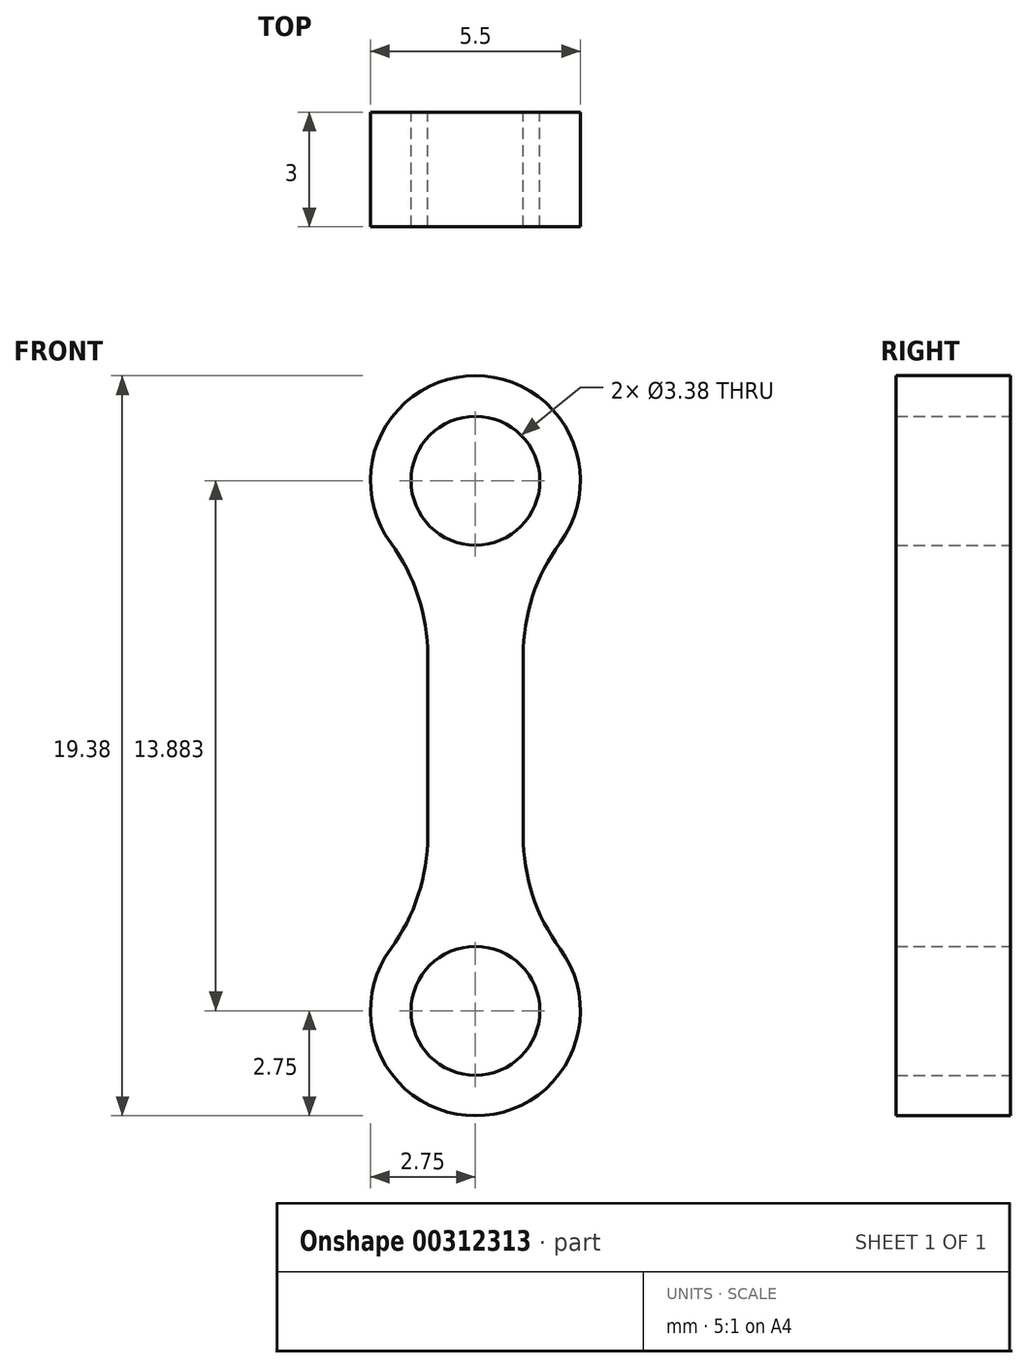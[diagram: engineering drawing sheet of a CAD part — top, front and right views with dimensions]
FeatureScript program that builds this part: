
annotation { "Feature Type Name" : "Feature", "Feature Type Description" : "" }
export const myFeature = defineFeature(function(context is Context, id is Id, definition is map)
    precondition{}
    {
        {
            var Q0;
            Q0=qCreatedBy(makeId("Front.planeOp"),FACE);
            var sketch = newSketch(context, id + "F0", { "sketchPlane" : qUnion([Q0])});
            skArc(sketch, "E0", {"start": v(-1.25, 2.45) * mm, "mid": v(0, -2.75) * mm, "end": v(1.25, 2.45) * mm});
            skCircle(sketch, "E1", {"center": v(0, 0) * mm, "radius": 1.69 * mm});
            skLineSegment(sketch, "E2", {"start": v(-1.25, 2.45) * mm, "end": v(-1.25, 11.43) * mm});
            skArc(sketch, "E3", {"start": v(1.25, 11.43) * mm, "mid": v(0, 16.63) * mm, "end": v(-1.25, 11.43) * mm});
            skCircle(sketch, "E4", {"center": v(0, 13.88) * mm, "radius": 1.69 * mm});
            skLineSegment(sketch, "E5.trimOffspring", {"start": v(1.25, 11.43) * mm, "end": v(1.25, 2.45) * mm});
            skPoint(sketch, "E6.trimOffspring.end.orphan", {"position": v(-0.7, 13.88) * mm});
            skPoint(sketch, "E7.start.orphan", {"position": v(0.7, 13.88) * mm});
            skSolve(sketch);
        }
        {
            var Q0;
            Q0=makeQuery(id+"F0.imprint","IMPRINT",FACE,{"disambiguationData":[TD([[makeQuery(id+"F0.imprint","IMPRINT",EDGE,{"derivedFrom":sQuery(id+"F0.wireOp",EDGE,"E0")}),1.0]])]});
            extrude(context, id + "F1", {"entities" : qUnion([Q0]), "depth" : 3 * mm});
        }
        {
            var Q0;
            Q0=makeQuery(id+"F1.opExtrude","SWEPT_EDGE",EDGE,{"disambiguationData":[OSD([sQuery(id+"F0.wireOp",EDGE,"E0"),sQuery(id+"F0.wireOp",EDGE,"E5.trimOffspring")])]});
            var Q1;
            Q1=makeQuery(id+"F1.opExtrude","SWEPT_EDGE",EDGE,{"disambiguationData":[OSD([sQuery(id+"F0.wireOp",EDGE,"E0"),sQuery(id+"F0.wireOp",EDGE,"E2")])]});
            var Q2;
            Q2=makeQuery(id+"F1.opExtrude","SWEPT_EDGE",EDGE,{"disambiguationData":[OSD([sQuery(id+"F0.wireOp",EDGE,"E2"),sQuery(id+"F0.wireOp",EDGE,"E3")])]});
            var Q3;
            Q3=makeQuery(id+"F1.opExtrude","SWEPT_EDGE",EDGE,{"disambiguationData":[OSD([sQuery(id+"F0.wireOp",EDGE,"E3"),sQuery(id+"F0.wireOp",EDGE,"E5.trimOffspring")])]});
            fillet(context, id + "F2", {"entities" : qUnion([Q0, Q1, Q2, Q3]), "radius" : 5 * mm, "tangentPropagation" : true, "allowEdgeOverflow" : false});
        }
    });
